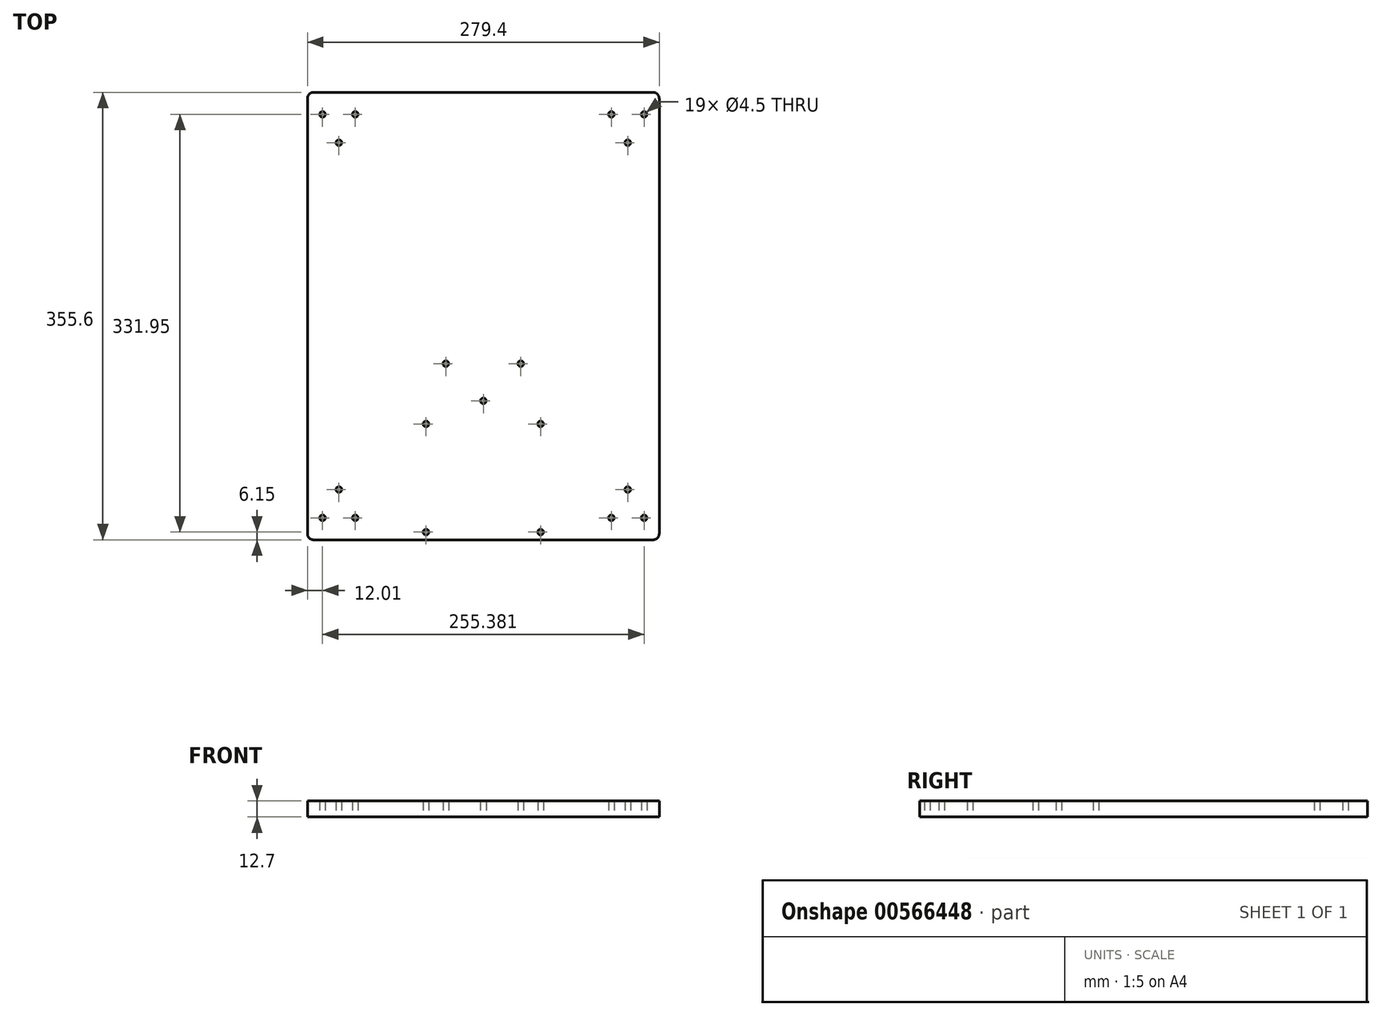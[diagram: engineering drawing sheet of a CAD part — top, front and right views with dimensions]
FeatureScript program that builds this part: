
annotation { "Feature Type Name" : "Feature", "Feature Type Description" : "" }
export const myFeature = defineFeature(function(context is Context, id is Id, definition is map)
    precondition{}
    {
        {
            var Q0;
            Q0=qCreatedBy(makeId("Top.planeOp"),FACE);
            var sketch = newSketch(context, id + "F0", { "sketchPlane" : qUnion([Q0])});
            skLineSegment(sketch, "E0.bottom", {"start": v(139.7, -177.8) * mm, "end": v(-139.7, -177.8) * mm});
            skLineSegment(sketch, "E0.top", {"start": v(139.7, 177.8) * mm, "end": v(-139.7, 177.8) * mm});
            skLineSegment(sketch, "E0.left", {"start": v(139.7, -177.8) * mm, "end": v(139.7, 177.8) * mm});
            skLineSegment(sketch, "E0.right", {"start": v(-139.7, -177.8) * mm, "end": v(-139.7, 177.8) * mm});
            skPoint(sketch, "E0.middle", {"position": v(0, 0) * mm});
            skCircle(sketch, "E1", {"center": v(-29.75, -37.8) * mm, "radius": 2.25 * mm});
            skCircle(sketch, "E2.MirrorC", {"center": v(29.75, -37.8) * mm, "radius": 2.25 * mm});
            skCircle(sketch, "E3", {"center": v(0, -67.3) * mm, "radius": 2.25 * mm});
            skCircle(sketch, "E4", {"center": v(-114.7, -137.8) * mm, "radius": 2.25 * mm});
            skCircle(sketch, "E5", {"center": v(-114.7, -152.8) * mm, "radius": 5 * mm, "construction": true});
            skCircle(sketch, "E6.1.0", {"center": v(-127.7, -160.3) * mm, "radius": 2.25 * mm});
            skCircle(sketch, "E6.2.0", {"center": v(-101.7, -160.3) * mm, "radius": 2.25 * mm});
            skCircle(sketch, "E7.MirrorC", {"center": v(114.7, -137.8) * mm, "radius": 2.25 * mm});
            skCircle(sketch, "E8.MirrorC", {"center": v(127.7, -160.3) * mm, "radius": 2.25 * mm});
            skCircle(sketch, "E9.MirrorC", {"center": v(101.7, -160.3) * mm, "radius": 2.25 * mm});
            skPoint(sketch, "E10.MirrorP", {"position": v(114.7, -152.8) * mm});
            skCircle(sketch, "E11.MirrorC", {"center": v(114.7, -152.8) * mm, "radius": 5 * mm, "construction": true});
            skCircle(sketch, "E12.MirrorC", {"center": v(-101.7, 160.3) * mm, "radius": 2.25 * mm});
            skCircle(sketch, "E13.MirrorC", {"center": v(-114.7, 137.8) * mm, "radius": 2.25 * mm});
            skPoint(sketch, "E14.MirrorP", {"position": v(-114.7, 152.8) * mm});
            skCircle(sketch, "E15.MirrorC", {"center": v(-114.7, 152.8) * mm, "radius": 5 * mm, "construction": true});
            skCircle(sketch, "E16.MirrorC", {"center": v(114.7, 137.8) * mm, "radius": 2.25 * mm});
            skCircle(sketch, "E17.MirrorC", {"center": v(101.7, 160.3) * mm, "radius": 2.25 * mm});
            skCircle(sketch, "E18.MirrorC", {"center": v(127.7, 160.3) * mm, "radius": 2.25 * mm});
            skPoint(sketch, "E19.MirrorP", {"position": v(114.7, 152.8) * mm});
            skCircle(sketch, "E20.MirrorC", {"center": v(114.7, 152.8) * mm, "radius": 5 * mm, "construction": true});
            skCircle(sketch, "E21.MirrorC", {"center": v(-127.7, 160.3) * mm, "radius": 2.25 * mm});
            skCircle(sketch, "E22", {"center": v(-45.5, -171.65) * mm, "radius": 2.25 * mm});
            skCircle(sketch, "E23.MirrorC", {"center": v(45.5, -171.65) * mm, "radius": 2.25 * mm});
            skLineSegment(sketch, "E24.bottom", {"start": v(45.5, -171.65) * mm, "end": v(-45.5, -171.65) * mm, "construction": true});
            skLineSegment(sketch, "E24.top", {"start": v(45.5, -85.65) * mm, "end": v(-45.5, -85.65) * mm, "construction": true});
            skLineSegment(sketch, "E24.left", {"start": v(45.5, -171.65) * mm, "end": v(45.5, -85.65) * mm, "construction": true});
            skLineSegment(sketch, "E24.right", {"start": v(-45.5, -171.65) * mm, "end": v(-45.5, -85.65) * mm, "construction": true});
            skPoint(sketch, "E24.middle", {"position": v(0, -128.65) * mm});
            skLineSegment(sketch, "E25", {"start": v(-45.5, -128.65) * mm, "end": v(45.5, -128.65) * mm, "construction": true});
            skCircle(sketch, "E26.MirrorC", {"center": v(-45.5, -85.65) * mm, "radius": 2.25 * mm});
            skCircle(sketch, "E27.MirrorC", {"center": v(45.5, -85.65) * mm, "radius": 2.25 * mm});
            skSolve(sketch);
        }
        {
            var Q0;
            Q0=qSketchRegion(id+"F0",true);
            extrude(context, id + "F1", {"entities" : qUnion([Q0]), "depth" : 12.7 * mm, "offsetDistance" : 25 * mm});
        }
        {
            var Q0;
            Q0=makeQuery(id+"F1.opExtrude","SWEPT_EDGE",EDGE,{"disambiguationData":[OSD([sQuery(id+"F0.wireOp",EDGE,"E0.bottom"),sQuery(id+"F0.wireOp",EDGE,"E0.right")])]});
            var Q1;
            Q1=makeQuery(id+"F1.opExtrude","SWEPT_EDGE",EDGE,{"disambiguationData":[OSD([sQuery(id+"F0.wireOp",EDGE,"E0.bottom"),sQuery(id+"F0.wireOp",EDGE,"E0.left")])]});
            var Q2;
            Q2=makeQuery(id+"F1.opExtrude","SWEPT_EDGE",EDGE,{"disambiguationData":[OSD([sQuery(id+"F0.wireOp",EDGE,"E0.top"),sQuery(id+"F0.wireOp",EDGE,"E0.left")])]});
            var Q3;
            Q3=makeQuery(id+"F1.opExtrude","SWEPT_EDGE",EDGE,{"disambiguationData":[OSD([sQuery(id+"F0.wireOp",EDGE,"E0.top"),sQuery(id+"F0.wireOp",EDGE,"E0.right")])]});
            fillet(context, id + "F2", {"entities" : qUnion([Q0, Q1, Q2, Q3]), "radius" : 5 * mm, "tangentPropagation" : true, "allowEdgeOverflow" : false});
        }
    });
